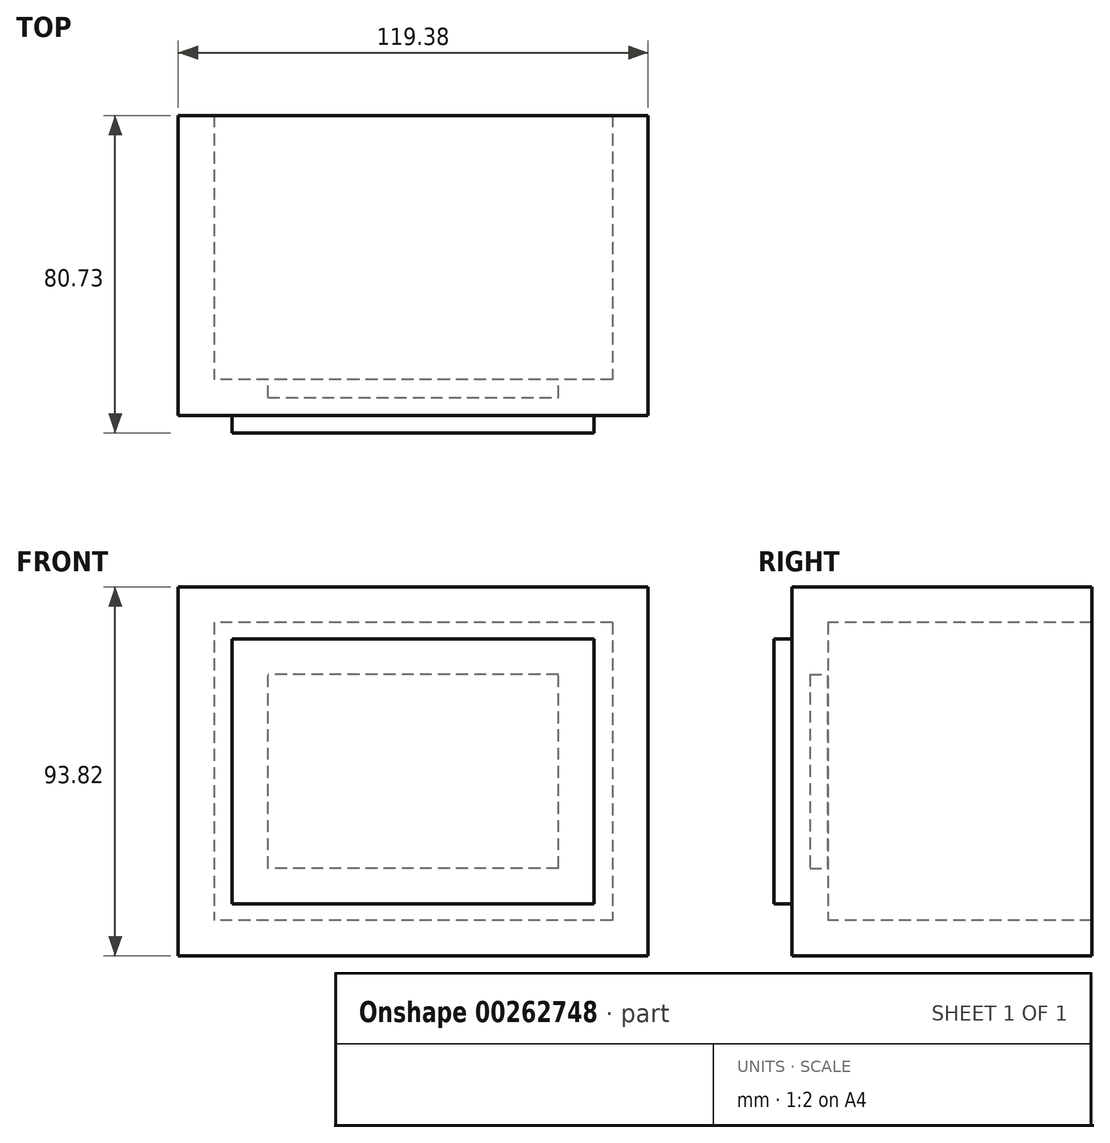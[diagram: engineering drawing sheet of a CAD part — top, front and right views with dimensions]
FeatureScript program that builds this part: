
annotation { "Feature Type Name" : "Feature", "Feature Type Description" : "" }
export const myFeature = defineFeature(function(context is Context, id is Id, definition is map)
    precondition{}
    {
        {
            var Q0;
            Q0=qCreatedBy(makeId("Top.planeOp"),FACE);
            var sketch = newSketch(context, id + "F0", { "sketchPlane" : qUnion([Q0])});
            skLineSegment(sketch, "E0.bottom", {"start": v(50.62, 33.56) * mm, "end": v(-50.62, 33.56) * mm});
            skLineSegment(sketch, "E0.top", {"start": v(50.62, -33.56) * mm, "end": v(-50.62, -33.56) * mm});
            skLineSegment(sketch, "E0.left", {"start": v(50.62, 33.56) * mm, "end": v(50.62, -33.56) * mm});
            skLineSegment(sketch, "E0.right", {"start": v(-50.62, 33.56) * mm, "end": v(-50.62, -33.56) * mm});
            skPoint(sketch, "E0.middle", {"position": v(0, 0) * mm});
            skLineSegment(sketch, "E1", {"start": v(-50.62, 33.56) * mm, "end": v(0, 11.37) * mm});
            skLineSegment(sketch, "E2", {"start": v(0, 11.37) * mm, "end": v(50.62, 33.56) * mm});
            skLineSegment(sketch, "E3", {"start": v(-50.62, -33.56) * mm, "end": v(0, -11.58) * mm});
            skLineSegment(sketch, "E4", {"start": v(0, -11.58) * mm, "end": v(50.62, -33.56) * mm});
            skLineSegment(sketch, "E5", {"start": v(0, 11.37) * mm, "end": v(0, -11.58) * mm});
            skSolve(sketch);
        }
        {
            var Q0;
            Q0=qCreatedBy(makeId("Front.planeOp"),FACE);
            var sketch = newSketch(context, id + "F1", { "sketchPlane" : qUnion([Q0])});
            skLineSegment(sketch, "E6.bottom", {"start": v(-36.9, 24.6) * mm, "end": v(36.9, 24.6) * mm});
            skLineSegment(sketch, "E6.top", {"start": v(-36.9, -24.6) * mm, "end": v(36.9, -24.6) * mm});
            skLineSegment(sketch, "E6.left", {"start": v(-36.9, 24.6) * mm, "end": v(-36.9, -24.6) * mm});
            skLineSegment(sketch, "E6.right", {"start": v(36.9, 24.6) * mm, "end": v(36.9, -24.6) * mm});
            skPoint(sketch, "E6.middle", {"position": v(0, 0) * mm});
            skSolve(sketch);
        }
        {
            var Q0;
            Q0=makeQuery(id+"F0.imprint","IMPRINT",FACE,{"disambiguationData":[TD([[makeQuery(id+"F0.imprint","IMPRINT",EDGE,{"derivedFrom":sQuery(id+"F0.wireOp",EDGE,"E0.left")}),-1.0]])]});
            var Q1;
            Q1=makeQuery(id+"F0.imprint","IMPRINT",FACE,{"disambiguationData":[TD([[makeQuery(id+"F0.imprint","IMPRINT",EDGE,{"derivedFrom":sQuery(id+"F0.wireOp",EDGE,"E0.right")}),1.0]])]});
            var Q2;
            Q2=makeQuery(id+"F0.imprint","IMPRINT",FACE,{"disambiguationData":[TD([[makeQuery(id+"F0.imprint","IMPRINT",EDGE,{"derivedFrom":sQuery(id+"F0.wireOp",EDGE,"E0.bottom")}),1.0]])]});
            var Q3;
            Q3=makeQuery(id+"F0.imprint","IMPRINT",FACE,{"disambiguationData":[TD([[makeQuery(id+"F0.imprint","IMPRINT",EDGE,{"derivedFrom":sQuery(id+"F0.wireOp",EDGE,"E0.top")}),-1.0]])]});
            extrude(context, id + "F2", {"entities" : qUnion([Q0, Q1, Q2, Q3]), "endBound" : BoundingType.SYMMETRIC, "depth" : 75.7 * mm});
        }
        {
            var Q0;
            Q0 = qSketchRegion(id + "F1", true);
            extrude(context, id + "F3", {"entities" : qUnion([Q0]), "operationType" : NewBodyOperationType.ADD, "depth" : 38.1 * mm});
        }
        {
            var Q0;
            Q0=makeQuery(id+"F2.opExtrude","SWEPT_FACE",FACE,{"disambiguationData":[OSD([sQuery(id+"F0.wireOp",EDGE,"E0.bottom")])]});
            shell(context, id + "F4", {"entities" : qUnion([Q0]), "thickness" : 9.07 * mm, "oppositeDirection" : true});
        }
    });
